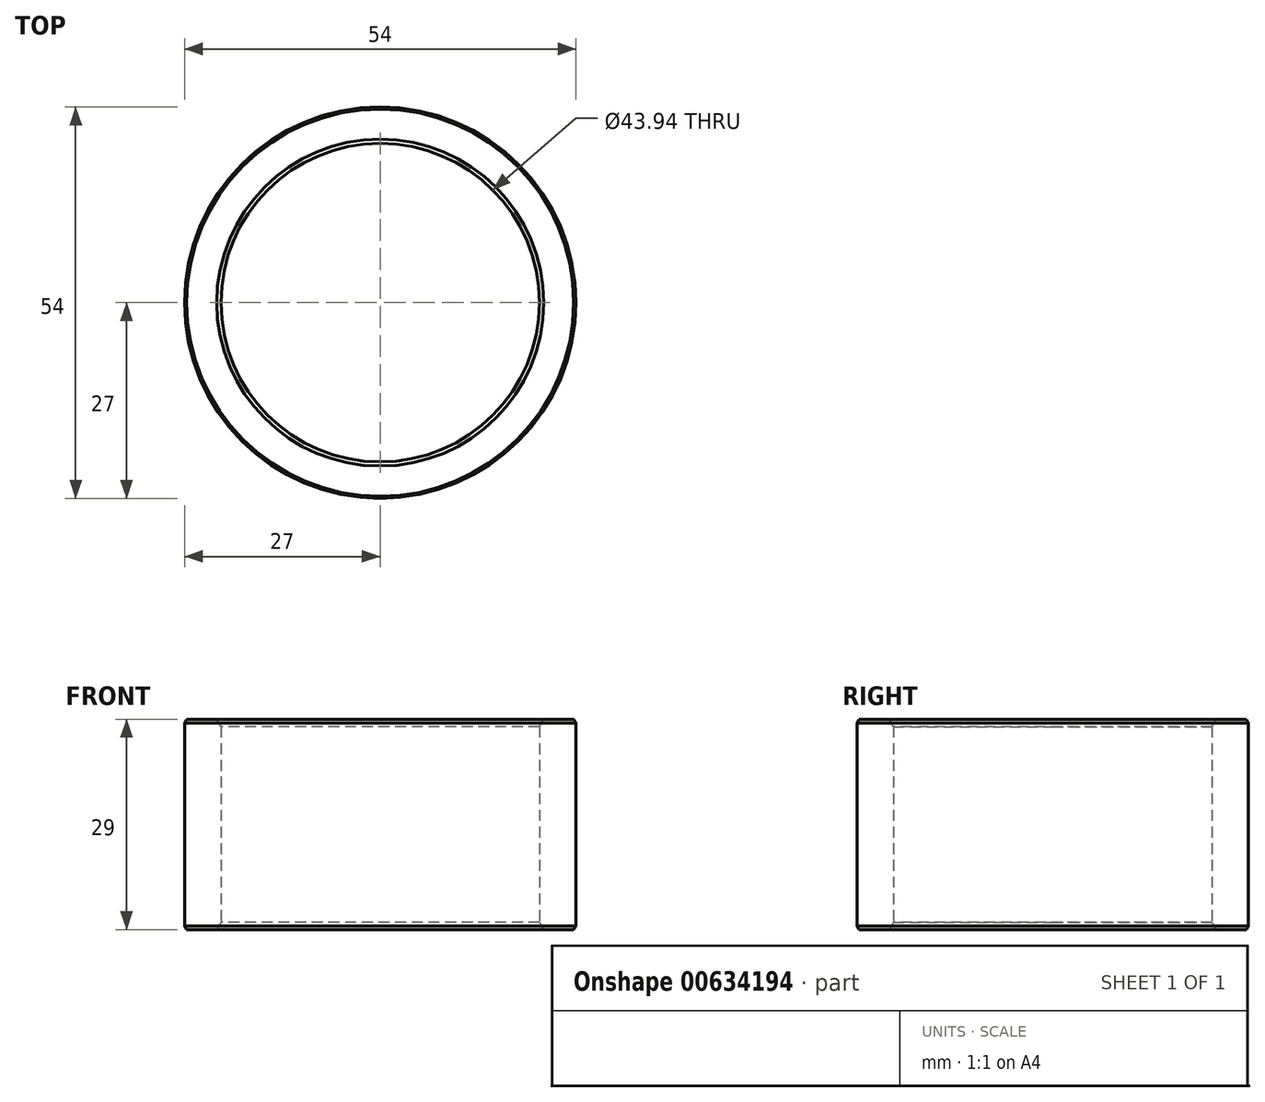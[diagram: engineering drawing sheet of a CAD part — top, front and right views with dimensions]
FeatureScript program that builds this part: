
annotation { "Feature Type Name" : "Feature", "Feature Type Description" : "" }
export const myFeature = defineFeature(function(context is Context, id is Id, definition is map)
    precondition{}
    {
        {
            var Q0;
            Q0=qCreatedBy(makeId("Top.planeOp"),FACE);
            var sketch = newSketch(context, id + "F0", { "sketchPlane" : qUnion([Q0])});
            skCircle(sketch, "E0", {"center": v(0, 0) * mm, "radius": 21.97 * mm});
            skCircle(sketch, "E1", {"center": v(0, 0) * mm, "radius": 27 * mm});
            skSolve(sketch);
        }
        {
            var Q0;
            Q0=makeQuery(id+"F0.imprint","IMPRINT",FACE,{"disambiguationData":[TD([[makeQuery(id+"F0.imprint","IMPRINT",EDGE,{"derivedFrom":sQuery(id+"F0.wireOp",EDGE,"E0")}),-1.0]])]});
            extrude(context, id + "F1", {"entities" : qUnion([Q0]), "depth" : 29 * mm, "offsetDistance" : 25 * mm});
        }
        {
            var Q0;
            Q0=makeQuery(id+"F1.opExtrude","CAP_EDGE",EDGE,{"disambiguationData":[OSD([sQuery(id+"F0.wireOp",EDGE,"E0")])],"isStart":false});
            var Q1;
            Q1=makeQuery(id+"F1.opExtrude","CAP_EDGE",EDGE,{"disambiguationData":[OSD([sQuery(id+"F0.wireOp",EDGE,"E0")])],"isStart":true});
            chamfer(context, id + "F2", {"entities" : qUnion([Q0, Q1]), "chamferType" : ChamferType.OFFSET_ANGLE, "width" : 1 * mm, "oppositeDirection" : false, "angle" : 30 * degree, "tangentPropagation" : true});
        }
        {
            var Q0;
            Q0=makeQuery(id+"F1.opExtrude","CAP_EDGE",EDGE,{"disambiguationData":[OSD([sQuery(id+"F0.wireOp",EDGE,"E1")])],"isStart":false});
            var Q1;
            Q1=makeQuery(id+"F1.opExtrude","CAP_EDGE",EDGE,{"disambiguationData":[OSD([sQuery(id+"F0.wireOp",EDGE,"E1")])],"isStart":true});
            chamfer(context, id + "F3", {"entities" : qUnion([Q0, Q1]), "chamferType" : ChamferType.OFFSET_ANGLE, "width" : 0.5 * mm, "oppositeDirection" : true, "angle" : 30 * degree, "tangentPropagation" : true});
        }
    });
